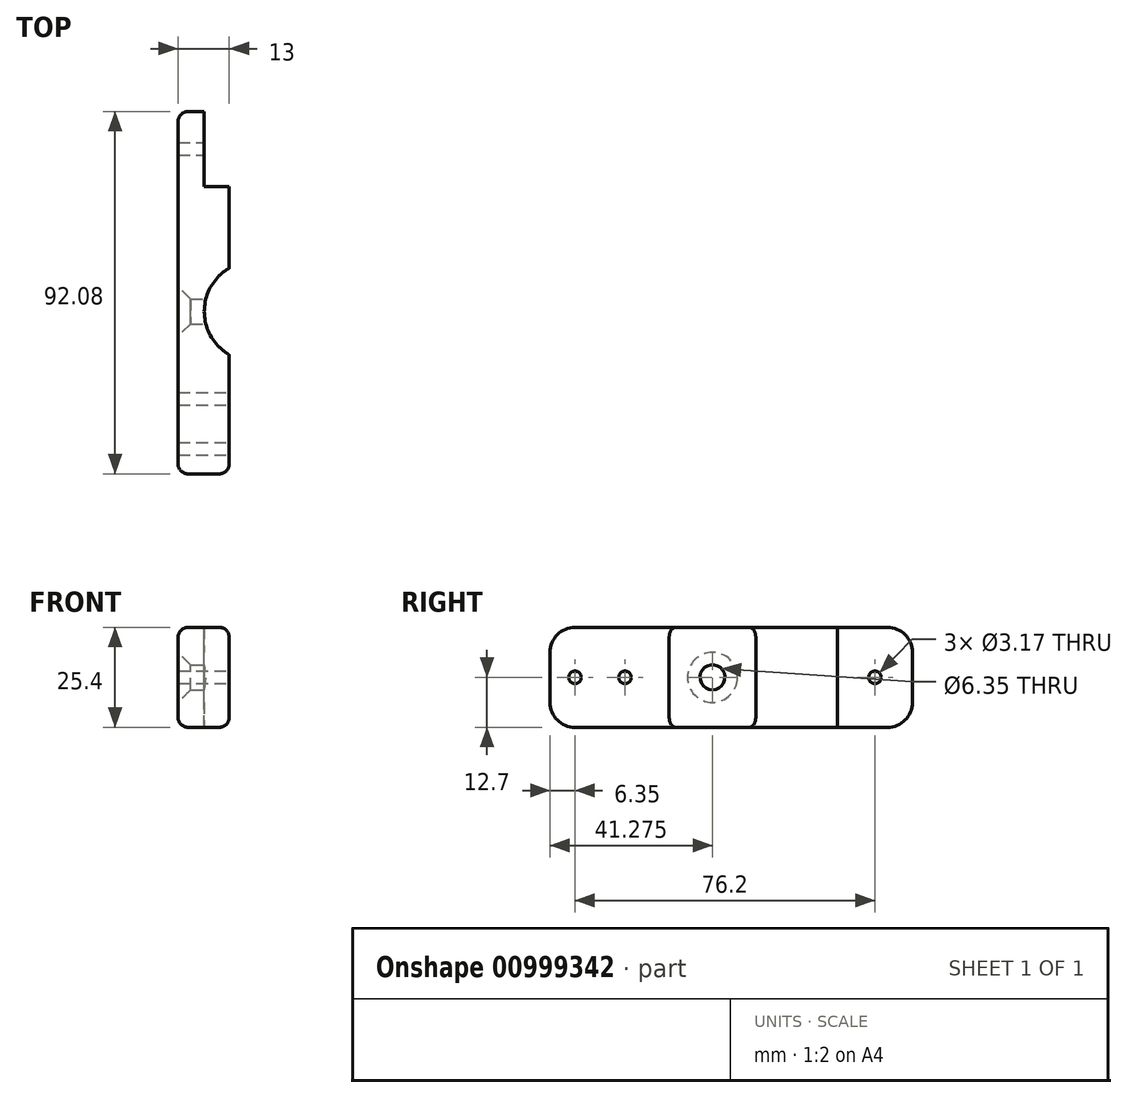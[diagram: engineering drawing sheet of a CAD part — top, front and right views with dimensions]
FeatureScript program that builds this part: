
annotation { "Feature Type Name" : "Feature", "Feature Type Description" : "" }
export const myFeature = defineFeature(function(context is Context, id is Id, definition is map)
    precondition{}
    {
        {
            var Q0;
            Q0=qCreatedBy(makeId("Right.planeOp"),FACE);
            var sketch = newSketch(context, id + "F0", { "sketchPlane" : qUnion([Q0])});
            skLineSegment(sketch, "E0", {"start": v(0, -12.7) * mm, "end": v(92.08, -12.7) * mm});
            skLineSegment(sketch, "E1", {"start": v(92.08, -12.7) * mm, "end": v(92.08, 0) * mm});
            skLineSegment(sketch, "E2.MirrorCS", {"start": v(0, 0) * mm, "end": v(0, 12.7) * mm});
            skLineSegment(sketch, "E3.MirrorCS", {"start": v(0, 12.7) * mm, "end": v(92.08, 12.7) * mm});
            skLineSegment(sketch, "E4.MirrorCS", {"start": v(92.08, 12.7) * mm, "end": v(92.08, 0) * mm});
            skCircle(sketch, "E5", {"center": v(82.55, 0) * mm, "radius": 1.59 * mm});
            skCircle(sketch, "E6.MirrorC", {"center": v(6.35, 0) * mm, "radius": 1.59 * mm});
            skCircle(sketch, "E7", {"center": v(41.27, 0) * mm, "radius": 3.18 * mm});
            skLineSegment(sketch, "E8", {"start": v(73.03, -12.7) * mm, "end": v(73.03, 12.7) * mm, "construction": true});
            skLineSegment(sketch, "E9.MirrorCS", {"start": v(0, 0) * mm, "end": v(0, -12.7) * mm});
            skLineSegment(sketch, "E10", {"start": v(28.57, 12.7) * mm, "end": v(28.57, -12.7) * mm, "construction": true});
            skCircle(sketch, "E11", {"center": v(19.05, 0) * mm, "radius": 1.59 * mm});
            skSolve(sketch);
        }
        {
            var Q0;
            Q0=qSketchRegion(id+"F0",true);
            extrude(context, id + "F1", {"entities" : qUnion([Q0]), "oppositeDirection" : true, "depth" : 13 * mm, "offsetDistance" : 25 * mm});
        }
        {
            var Q0;
            Q0=qCreatedBy(makeId("Top.planeOp"),FACE);
            var sketch = newSketch(context, id + "F2", { "sketchPlane" : qUnion([Q0])});
            skArc(sketch, "E12", {"start": v(0, 52.27) * mm, "mid": v(-6.35, 41.27) * mm, "end": v(0, 30.28) * mm});
            skLineSegment(sketch, "E13", {"start": v(0, 30.28) * mm, "end": v(0, 52.27) * mm});
            skLineSegment(sketch, "E14.bottom", {"start": v(0, 92.08) * mm, "end": v(-6.35, 92.08) * mm});
            skLineSegment(sketch, "E14.top", {"start": v(0, 73.03) * mm, "end": v(-6.35, 73.03) * mm});
            skLineSegment(sketch, "E14.left", {"start": v(0, 92.08) * mm, "end": v(0, 73.03) * mm});
            skLineSegment(sketch, "E14.right", {"start": v(-6.35, 92.08) * mm, "end": v(-6.35, 73.03) * mm});
            skSolve(sketch);
        }
        {
            var Q0;
            Q0=qSketchRegion(id+"F2",true);
            extrude(context, id + "F3", {"entities" : qUnion([Q0]), "operationType" : NewBodyOperationType.REMOVE, "endBound" : BoundingType.SYMMETRIC, "oppositeDirection" : true, "depth" : 75 * mm, "offsetDistance" : 25 * mm});
        }
        {
            var Q0;
            Q0=makeQuery(id+"F1.opExtrude","SWEPT_EDGE",EDGE,{"disambiguationData":[OSD([sQuery(id+"F0.wireOp",EDGE,"d868d885-708a-4358-ac4c-7e472c41f0fd2.MirrorCS"),sQuery(id+"F0.wireOp",EDGE,"d868d885-708a-4358-ac4c-7e472c41f0fd4.MirrorCS")])]});
            var Q1;
            Q1=makeQuery(id+"F1.opExtrude","SWEPT_EDGE",EDGE,{"disambiguationData":[OSD([sQuery(id+"F0.wireOp",EDGE,"E3.MirrorCS"),sQuery(id+"F0.wireOp",EDGE,"d868d885-708a-4358-ac4c-7e472c41f0fd4.MirrorCS")])]});
            var Q2;
            Q2=makeQuery(id+"F1.opExtrude","SWEPT_EDGE",EDGE,{"disambiguationData":[OSD([sQuery(id+"F0.wireOp",EDGE,"g0e7l1pj-qA0Y-fhNS-CB5I-AUhqAXy8HTwi"),sQuery(id+"F0.wireOp",EDGE,"E0")])]});
            var Q3;
            Q3=makeQuery(id+"F1.opExtrude","SWEPT_EDGE",EDGE,{"disambiguationData":[OSD([sQuery(id+"F0.wireOp",EDGE,"wscSROFl-acIJ-EUQi-56bg-9ylbmSFamOZR"),sQuery(id+"F0.wireOp",EDGE,"g0e7l1pj-qA0Y-fhNS-CB5I-AUhqAXy8HTwi")])]});
            fillet(context, id + "F4", {"entities" : qUnion([Q0, Q1, Q2, Q3]), "radius" : 6.35 * mm, "tangentPropagation" : true, "defaultsChanged" : true, "vertexSettings" : [], "allowEdgeOverflow" : false});
        }
        {
            var Q0;
            Q0=makeQuery(id+"F1.opExtrude","CAP_EDGE",EDGE,{"disambiguationData":[OSD([sQuery(id+"F0.wireOp",EDGE,"E1"),sQuery(id+"F0.wireOp",EDGE,"E4.MirrorCS")])],"isStart":false});
            var Q1;
            Q1=makeQuery(id+"F1.opExtrude","CAP_EDGE",EDGE,{"disambiguationData":[OSD([sQuery(id+"F0.wireOp",EDGE,"j31KRHDU-dVKS-fmwK-bgvL-qThiKXJEA8MT"),sQuery(id+"F0.wireOp",EDGE,"E2.MirrorCS")])],"isStart":true});
            var Q2;
            {var subQ0=sQuery(id+"F0.wireOp",EDGE,"E3.MirrorCS");Q2=makeQuery(id+"F3.boolean.opBoolean","SPLIT",EDGE,{"disambiguationData":[TD([makeQuery(id+"F3.opExtrude","SWEPT_FACE",FACE,{"disambiguationData":[OSD([sQuery(id+"F2.wireOp",EDGE,"E14.top")])]})])],"derivedFrom":makeQuery(id+"F1.opExtrude","CAP_EDGE",EDGE,{"disambiguationData":[OSD([subQ0])],"isStart":true})});}
            var Q3;
            {var subQ0=sQuery(id+"F0.wireOp",EDGE,"E0");Q3=makeQuery(id+"F3.boolean.opBoolean","SPLIT",EDGE,{"disambiguationData":[TD([makeQuery(id+"F3.opExtrude","SWEPT_FACE",FACE,{"disambiguationData":[OSD([sQuery(id+"F2.wireOp",EDGE,"E14.top")])]})])],"derivedFrom":makeQuery(id+"F1.opExtrude","CAP_EDGE",EDGE,{"disambiguationData":[OSD([subQ0])],"isStart":true})});}
            fillet(context, id + "F5", {"entities" : qUnion([Q0, Q1, Q2, Q3]), "radius" : 2.54 * mm, "tangentPropagation" : true, "defaultsChanged" : false, "vertexSettings" : [], "allowEdgeOverflow" : false});
        }
        {
            var Q0;
            Q0=makeQuery(id+"F1.opExtrude","CAP_EDGE",EDGE,{"disambiguationData":[OSD([sQuery(id+"F0.wireOp",EDGE,"E7")])],"isStart":false});
            chamfer(context, id + "F6", {"entities" : qUnion([Q0]), "width" : 3.17 * mm, "tangentPropagation" : true});
        }
    });
